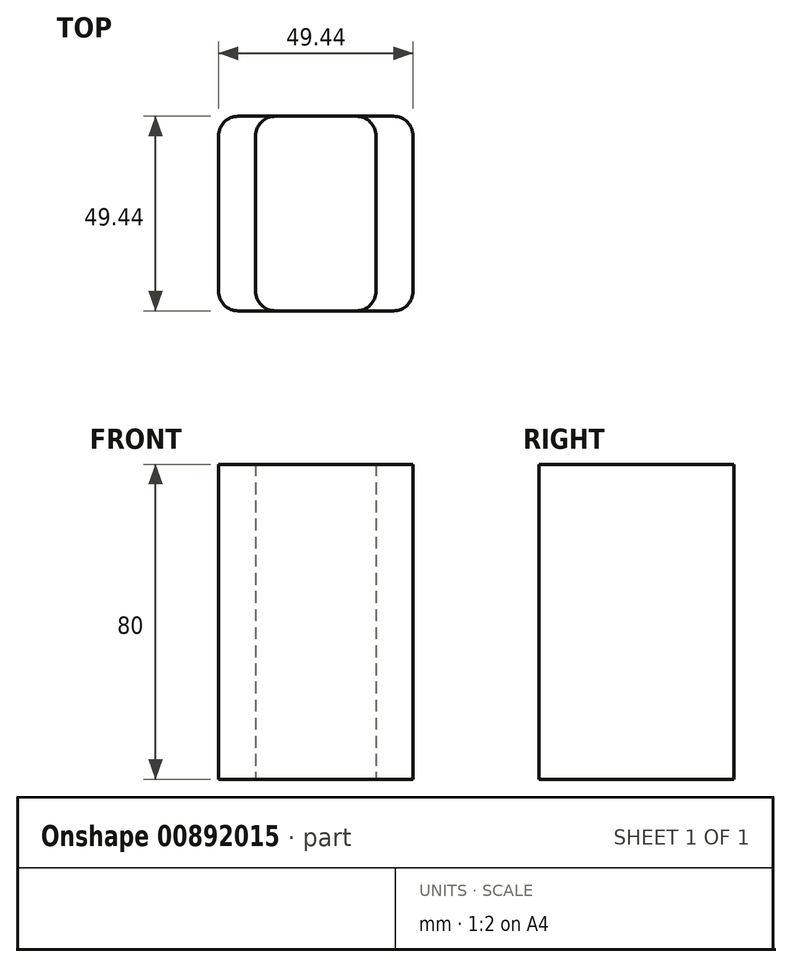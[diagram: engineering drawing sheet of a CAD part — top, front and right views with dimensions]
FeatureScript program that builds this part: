
annotation { "Feature Type Name" : "Feature", "Feature Type Description" : "" }
export const myFeature = defineFeature(function(context is Context, id is Id, definition is map)
    precondition{}
    {
        {
            var Q0;
            Q0=qCreatedBy(makeId("Top.planeOp"),FACE);
            var sketch = newSketch(context, id + "F0", { "sketchPlane" : qUnion([Q0])});
            skLineSegment(sketch, "E0.bottom", {"start": v(24.72, -24.72) * mm, "end": v(-24.72, -24.72) * mm});
            skLineSegment(sketch, "E0.top", {"start": v(24.72, 24.72) * mm, "end": v(-24.72, 24.72) * mm});
            skLineSegment(sketch, "E0.left", {"start": v(24.72, -24.72) * mm, "end": v(24.72, 24.72) * mm});
            skLineSegment(sketch, "E0.right", {"start": v(-24.72, -24.72) * mm, "end": v(-24.72, 24.72) * mm});
            skPoint(sketch, "E0.middle", {"position": v(0, 0) * mm});
            skSolve(sketch);
        }
        {
            var Q0;
            Q0 = qSketchRegion(id + "F0", true);
            extrude(context, id + "F1", {"entities" : qUnion([Q0]), "depth" : 80 * mm, "offsetDistance" : 25 * mm});
        }
        {
            var Q0;
            Q0=makeQuery(id+"F1.opExtrude","SWEPT_EDGE",EDGE,{"disambiguationData":[OSD([sQuery(id+"F0.wireOp",EDGE,"E0.top"),sQuery(id+"F0.wireOp",EDGE,"E0.right")])]});
            var Q1;
            Q1=makeQuery(id+"F1.opExtrude","SWEPT_EDGE",EDGE,{"disambiguationData":[OSD([sQuery(id+"F0.wireOp",EDGE,"E0.bottom"),sQuery(id+"F0.wireOp",EDGE,"E0.right")])]});
            var Q2;
            Q2=makeQuery(id+"F1.opExtrude","SWEPT_EDGE",EDGE,{"disambiguationData":[OSD([sQuery(id+"F0.wireOp",EDGE,"E0.bottom"),sQuery(id+"F0.wireOp",EDGE,"E0.left")])]});
            var Q3;
            Q3=makeQuery(id+"F1.opExtrude","SWEPT_EDGE",EDGE,{"disambiguationData":[OSD([sQuery(id+"F0.wireOp",EDGE,"E0.top"),sQuery(id+"F0.wireOp",EDGE,"E0.left")])]});
            fillet(context, id + "F2", {"entities" : qUnion([Q0, Q1, Q2, Q3]), "radius" : 5 * mm, "tangentPropagation" : true, "allowEdgeOverflow" : false});
        }
        {
            var Q0;
            Q0=qCreatedBy(makeId("Top.planeOp"),FACE);
            var sketch = newSketch(context, id + "F3", { "sketchPlane" : qUnion([Q0])});
            skLineSegment(sketch, "E1.bottom", {"start": v(15.28, -24.72) * mm, "end": v(-15.28, -24.72) * mm});
            skLineSegment(sketch, "E1.top", {"start": v(15.28, 24.72) * mm, "end": v(-15.28, 24.72) * mm});
            skLineSegment(sketch, "E1.left", {"start": v(15.28, -24.72) * mm, "end": v(15.28, 24.72) * mm});
            skLineSegment(sketch, "E1.right", {"start": v(-15.28, -24.72) * mm, "end": v(-15.28, 24.72) * mm});
            skPoint(sketch, "E1.middle", {"position": v(0, 0) * mm});
            skSolve(sketch);
        }
        {
            var Q0;
            Q0 = qSketchRegion(id + "F3", true);
            extrude(context, id + "F4", {"entities" : qUnion([Q0]), "depth" : 80 * mm, "offsetDistance" : 25 * mm});
        }
        {
            var Q0;
            Q0=makeQuery(id+"F4.opExtrude","SWEPT_EDGE",EDGE,{"disambiguationData":[OSD([sQuery(id+"F3.wireOp",EDGE,"E1.bottom"),sQuery(id+"F3.wireOp",EDGE,"E1.right")])]});
            var Q1;
            Q1=makeQuery(id+"F4.opExtrude","SWEPT_EDGE",EDGE,{"disambiguationData":[OSD([sQuery(id+"F3.wireOp",EDGE,"E1.bottom"),sQuery(id+"F3.wireOp",EDGE,"E1.left")])]});
            var Q2;
            Q2=makeQuery(id+"F4.opExtrude","SWEPT_EDGE",EDGE,{"disambiguationData":[OSD([sQuery(id+"F3.wireOp",EDGE,"E1.top"),sQuery(id+"F3.wireOp",EDGE,"E1.left")])]});
            var Q3;
            Q3=makeQuery(id+"F4.opExtrude","SWEPT_EDGE",EDGE,{"disambiguationData":[OSD([sQuery(id+"F3.wireOp",EDGE,"E1.top"),sQuery(id+"F3.wireOp",EDGE,"E1.right")])]});
            fillet(context, id + "F5", {"entities" : qUnion([Q0, Q1, Q2, Q3]), "radius" : 5 * mm, "tangentPropagation" : true, "allowEdgeOverflow" : false});
        }
    });
